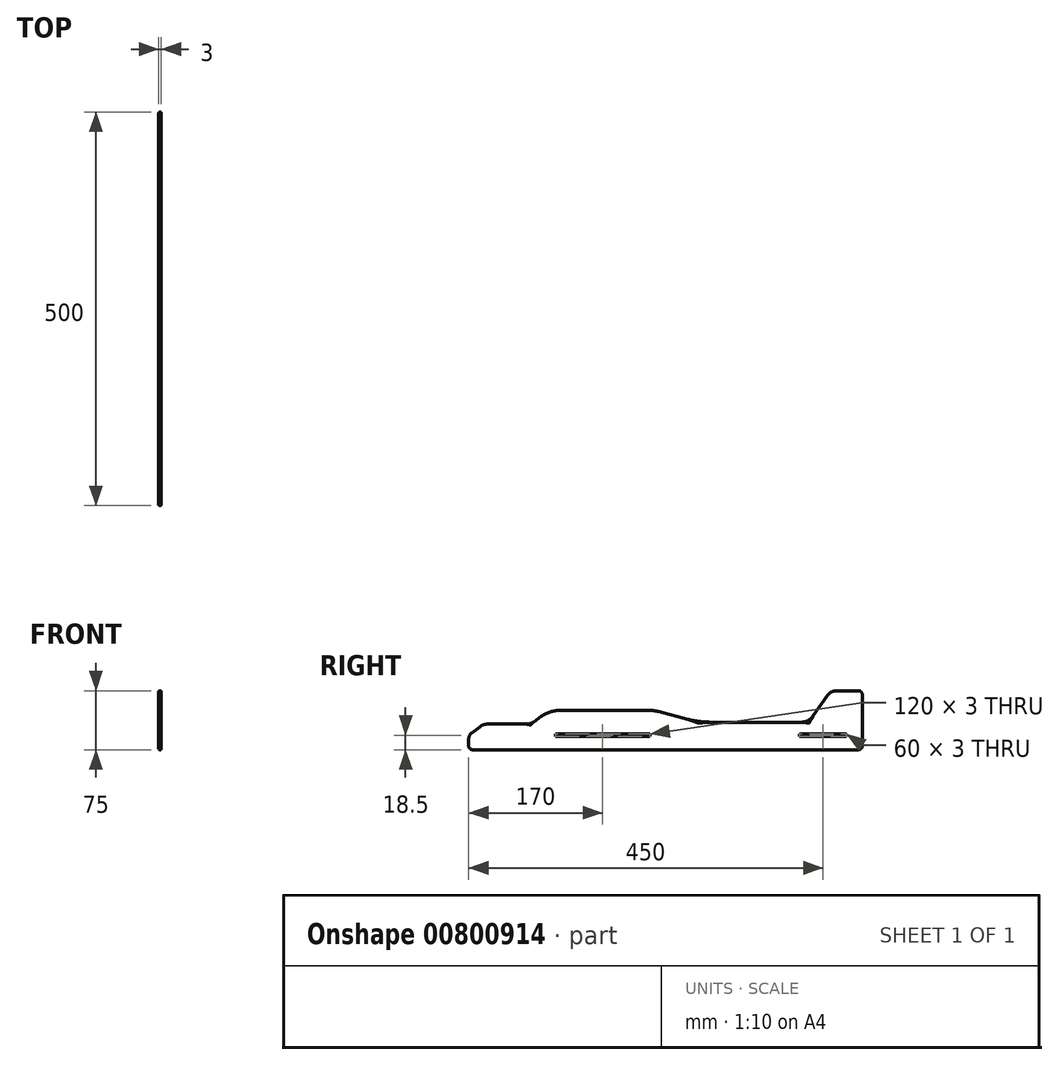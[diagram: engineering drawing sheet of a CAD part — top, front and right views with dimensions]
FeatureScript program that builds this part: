
annotation { "Feature Type Name" : "Feature", "Feature Type Description" : "" }
export const myFeature = defineFeature(function(context is Context, id is Id, definition is map)
    precondition{}
    {
        {
            var Q0;
            Q0=qCreatedBy(makeId("Right.planeOp"),FACE);
            var sketch = newSketch(context, id + "F0", { "sketchPlane" : qUnion([Q0])});
            skLineSegment(sketch, "E0.bottom", {"start": v(60, -1.5) * mm, "end": v(-60, -1.5) * mm});
            skLineSegment(sketch, "E0.top", {"start": v(60, 1.5) * mm, "end": v(-60, 1.5) * mm});
            skLineSegment(sketch, "E0.left", {"start": v(60, -1.5) * mm, "end": v(60, 1.5) * mm});
            skLineSegment(sketch, "E0.right", {"start": v(-60, -1.5) * mm, "end": v(-60, 1.5) * mm});
            skPoint(sketch, "E0.middle", {"position": v(0, 0) * mm});
            skLineSegment(sketch, "E1", {"start": v(-170, -18.5) * mm, "end": v(330, -18.5) * mm});
            skLineSegment(sketch, "E2", {"start": v(-170, -18.5) * mm, "end": v(-170, 0) * mm});
            skLineSegment(sketch, "E3", {"start": v(330, 56.5) * mm, "end": v(330, -18.5) * mm});
            skLineSegment(sketch, "E4", {"start": v(330, 56.5) * mm, "end": v(290, 56.5) * mm});
            skPoint(sketch, "E5.1.internal.snap0", {"position": v(330, 19) * mm});
            skLineSegment(sketch, "E6", {"start": v(290, 56.5) * mm, "end": v(262, 16.5) * mm});
            skLineSegment(sketch, "E7", {"start": v(262, 16.5) * mm, "end": v(122, 16.5) * mm});
            skLineSegment(sketch, "E8", {"start": v(122, 16.5) * mm, "end": v(65.33, 31.5) * mm});
            skLineSegment(sketch, "E9", {"start": v(65.33, 31.5) * mm, "end": v(-67.04, 31.5) * mm});
            skLineSegment(sketch, "E10", {"start": v(-67.04, 31.5) * mm, "end": v(-91.43, 14.03) * mm});
            skLineSegment(sketch, "E11", {"start": v(-91.43, 14.03) * mm, "end": v(-151.43, 14.03) * mm});
            skLineSegment(sketch, "E12", {"start": v(-151.43, 14.03) * mm, "end": v(-170, 0) * mm});
            skLineSegment(sketch, "E13.bottom", {"start": v(250, -1.5) * mm, "end": v(310, -1.5) * mm});
            skLineSegment(sketch, "E13.top", {"start": v(250, 1.5) * mm, "end": v(310, 1.5) * mm});
            skLineSegment(sketch, "E13.left", {"start": v(250, -1.5) * mm, "end": v(250, 1.5) * mm});
            skLineSegment(sketch, "E13.right", {"start": v(310, -1.5) * mm, "end": v(310, 1.5) * mm});
            skPoint(sketch, "E13.middle", {"position": v(280, 0) * mm});
            skSolve(sketch);
        }
        {
            var Q0;
            Q0=makeQuery(id+"F0.imprint","IMPRINT",FACE,{"disambiguationData":[TD([[makeQuery(id+"F0.imprint","IMPRINT",EDGE,{"derivedFrom":sQuery(id+"F0.wireOp",EDGE,"E0.bottom")}),1.0]])]});
            extrude(context, id + "F1", {"entities" : qUnion([Q0]), "endBound" : BoundingType.SYMMETRIC, "depth" : 3 * mm, "offsetDistance" : 25 * mm});
        }
        {
            var Q0;
            Q0=makeQuery(id+"F1.opExtrude","CAP_EDGE",EDGE,{"disambiguationData":[OSD([sQuery(id+"F0.wireOp",EDGE,"E8")])],"isStart":true});
            var Q1;
            Q1=makeQuery(id+"F1.opExtrude","CAP_EDGE",EDGE,{"disambiguationData":[OSD([sQuery(id+"F0.wireOp",EDGE,"E8")])],"isStart":false});
            var Q2;
            Q2=makeQuery(id+"F1.opExtrude","CAP_EDGE",EDGE,{"disambiguationData":[OSD([sQuery(id+"F0.wireOp",EDGE,"E7")])],"isStart":false});
            var Q3;
            Q3=makeQuery(id+"F1.opExtrude","CAP_EDGE",EDGE,{"disambiguationData":[OSD([sQuery(id+"F0.wireOp",EDGE,"E7")])],"isStart":true});
            var Q4;
            Q4=makeQuery(id+"F1.opExtrude","CAP_EDGE",EDGE,{"disambiguationData":[OSD([sQuery(id+"F0.wireOp",EDGE,"E6")])],"isStart":false});
            var Q5;
            Q5=makeQuery(id+"F1.opExtrude","CAP_EDGE",EDGE,{"disambiguationData":[OSD([sQuery(id+"F0.wireOp",EDGE,"E6")])],"isStart":true});
            var Q6;
            Q6=makeQuery(id+"F1.opExtrude","CAP_EDGE",EDGE,{"disambiguationData":[OSD([sQuery(id+"F0.wireOp",EDGE,"E4")])],"isStart":true});
            var Q7;
            Q7=makeQuery(id+"F1.opExtrude","CAP_EDGE",EDGE,{"disambiguationData":[OSD([sQuery(id+"F0.wireOp",EDGE,"E4")])],"isStart":false});
            var Q8;
            Q8=makeQuery(id+"F1.opExtrude","CAP_EDGE",EDGE,{"disambiguationData":[OSD([sQuery(id+"F0.wireOp",EDGE,"E3")])],"isStart":true});
            var Q9;
            Q9=makeQuery(id+"F1.opExtrude","CAP_EDGE",EDGE,{"disambiguationData":[OSD([sQuery(id+"F0.wireOp",EDGE,"E3")])],"isStart":false});
            var Q10;
            Q10=makeQuery(id+"F1.opExtrude","CAP_EDGE",EDGE,{"disambiguationData":[OSD([sQuery(id+"F0.wireOp",EDGE,"E1")])],"isStart":true});
            var Q11;
            Q11=makeQuery(id+"F1.opExtrude","CAP_EDGE",EDGE,{"disambiguationData":[OSD([sQuery(id+"F0.wireOp",EDGE,"E1")])],"isStart":false});
            var Q12;
            Q12=makeQuery(id+"F1.opExtrude","CAP_EDGE",EDGE,{"disambiguationData":[OSD([sQuery(id+"F0.wireOp",EDGE,"E9")])],"isStart":false});
            var Q13;
            Q13=makeQuery(id+"F1.opExtrude","CAP_EDGE",EDGE,{"disambiguationData":[OSD([sQuery(id+"F0.wireOp",EDGE,"E11")])],"isStart":false});
            var Q14;
            Q14=makeQuery(id+"F1.opExtrude","CAP_EDGE",EDGE,{"disambiguationData":[OSD([sQuery(id+"F0.wireOp",EDGE,"E12")])],"isStart":false});
            var Q15;
            Q15=makeQuery(id+"F1.opExtrude","CAP_EDGE",EDGE,{"disambiguationData":[OSD([sQuery(id+"F0.wireOp",EDGE,"E9")])],"isStart":true});
            var Q16;
            Q16=makeQuery(id+"F1.opExtrude","CAP_EDGE",EDGE,{"disambiguationData":[OSD([sQuery(id+"F0.wireOp",EDGE,"E10")])],"isStart":true});
            var Q17;
            Q17=makeQuery(id+"F1.opExtrude","CAP_EDGE",EDGE,{"disambiguationData":[OSD([sQuery(id+"F0.wireOp",EDGE,"E11")])],"isStart":true});
            var Q18;
            Q18=makeQuery(id+"F1.opExtrude","CAP_EDGE",EDGE,{"disambiguationData":[OSD([sQuery(id+"F0.wireOp",EDGE,"E12")])],"isStart":true});
            var Q19;
            Q19=makeQuery(id+"F1.opExtrude","CAP_EDGE",EDGE,{"disambiguationData":[OSD([sQuery(id+"F0.wireOp",EDGE,"E10")])],"isStart":false});
            var Q20;
            Q20=makeQuery(id+"F1.opExtrude","CAP_EDGE",EDGE,{"disambiguationData":[OSD([sQuery(id+"F0.wireOp",EDGE,"E2")])],"isStart":true});
            var Q21;
            Q21=makeQuery(id+"F1.opExtrude","CAP_EDGE",EDGE,{"disambiguationData":[OSD([sQuery(id+"F0.wireOp",EDGE,"E2")])],"isStart":false});
            fillet(context, id + "F2", {"entities" : qUnion([Q0, Q1, Q2, Q3, Q4, Q5, Q6, Q7, Q8, Q9, Q10, Q11, Q12, Q13, Q14, Q15, Q16, Q17, Q18, Q19, Q20, Q21]), "radius" : 1 * mm, "tangentPropagation" : true, "allowEdgeOverflow" : false});
        }
        {
            var Q0;
            Q0=makeQuery(id+"F1.opExtrude","SWEPT_EDGE",EDGE,{"disambiguationData":[OSD([sQuery(id+"F0.wireOp",EDGE,"E9"),sQuery(id+"F0.wireOp",EDGE,"E10")])]});
            fillet(context, id + "F3", {"entities" : qUnion([Q0]), "radius" : 41.74 * mm, "tangentPropagation" : true, "allowEdgeOverflow" : false});
        }
        {
            var Q0;
            Q0=makeQuery(id+"F1.opExtrude","SWEPT_EDGE",EDGE,{"disambiguationData":[OSD([sQuery(id+"F0.wireOp",EDGE,"E10"),sQuery(id+"F0.wireOp",EDGE,"E11")])]});
            fillet(context, id + "F4", {"entities" : qUnion([Q0]), "radius" : 15.9 * mm, "tangentPropagation" : true, "allowEdgeOverflow" : false});
        }
        {
            var Q0;
            Q0=makeQuery(id+"F1.opExtrude","SWEPT_EDGE",EDGE,{"disambiguationData":[OSD([sQuery(id+"F0.wireOp",EDGE,"E11"),sQuery(id+"F0.wireOp",EDGE,"E12")])]});
            fillet(context, id + "F5", {"entities" : qUnion([Q0]), "radius" : 16.44 * mm, "tangentPropagation" : true, "allowEdgeOverflow" : false});
        }
        {
            var Q0;
            Q0=makeQuery(id+"F1.opExtrude","SWEPT_EDGE",EDGE,{"disambiguationData":[OSD([sQuery(id+"F0.wireOp",EDGE,"E2"),sQuery(id+"F0.wireOp",EDGE,"E12")])]});
            fillet(context, id + "F6", {"entities" : qUnion([Q0]), "radius" : 10.25 * mm, "tangentPropagation" : true, "allowEdgeOverflow" : false});
        }
        {
            var Q0;
            Q0=makeQuery(id+"F1.opExtrude","SWEPT_EDGE",EDGE,{"disambiguationData":[OSD([sQuery(id+"F0.wireOp",EDGE,"E1"),sQuery(id+"F0.wireOp",EDGE,"E2")])]});
            fillet(context, id + "F7", {"entities" : qUnion([Q0]), "radius" : 5 * mm, "tangentPropagation" : true, "allowEdgeOverflow" : false});
        }
        {
            var Q0;
            Q0=makeQuery(id+"F1.opExtrude","SWEPT_EDGE",EDGE,{"disambiguationData":[OSD([sQuery(id+"F0.wireOp",EDGE,"E8"),sQuery(id+"F0.wireOp",EDGE,"E9")])]});
            fillet(context, id + "F8", {"entities" : qUnion([Q0]), "radius" : 47.45 * mm, "tangentPropagation" : true, "allowEdgeOverflow" : false});
        }
        {
            var Q0;
            Q0=makeQuery(id+"F1.opExtrude","SWEPT_EDGE",EDGE,{"disambiguationData":[OSD([sQuery(id+"F0.wireOp",EDGE,"E7"),sQuery(id+"F0.wireOp",EDGE,"E8")])]});
            fillet(context, id + "F9", {"entities" : qUnion([Q0]), "radius" : 106.77 * mm, "tangentPropagation" : true, "allowEdgeOverflow" : false});
        }
        {
            var Q0;
            Q0=makeQuery(id+"F1.opExtrude","SWEPT_EDGE",EDGE,{"disambiguationData":[OSD([sQuery(id+"F0.wireOp",EDGE,"E6"),sQuery(id+"F0.wireOp",EDGE,"E7")])]});
            fillet(context, id + "F10", {"entities" : qUnion([Q0]), "radius" : 18.06 * mm, "tangentPropagation" : true, "allowEdgeOverflow" : false});
        }
        {
            var Q0;
            Q0=makeQuery(id+"F1.opExtrude","SWEPT_EDGE",EDGE,{"disambiguationData":[OSD([sQuery(id+"F0.wireOp",EDGE,"E4"),sQuery(id+"F0.wireOp",EDGE,"E6")])]});
            fillet(context, id + "F11", {"entities" : qUnion([Q0]), "radius" : 14.13 * mm, "tangentPropagation" : true, "allowEdgeOverflow" : false});
        }
        {
            var Q0;
            Q0=makeQuery(id+"F1.opExtrude","SWEPT_EDGE",EDGE,{"disambiguationData":[OSD([sQuery(id+"F0.wireOp",EDGE,"E3"),sQuery(id+"F0.wireOp",EDGE,"E4")])]});
            fillet(context, id + "F12", {"entities" : qUnion([Q0]), "radius" : 5 * mm, "tangentPropagation" : true, "allowEdgeOverflow" : false});
        }
        {
            var Q0;
            Q0=makeQuery(id+"F1.opExtrude","SWEPT_EDGE",EDGE,{"disambiguationData":[OSD([sQuery(id+"F0.wireOp",EDGE,"E1"),sQuery(id+"F0.wireOp",EDGE,"E3")])]});
            fillet(context, id + "F13", {"entities" : qUnion([Q0]), "radius" : 5 * mm, "tangentPropagation" : true, "allowEdgeOverflow" : false});
        }
    });
